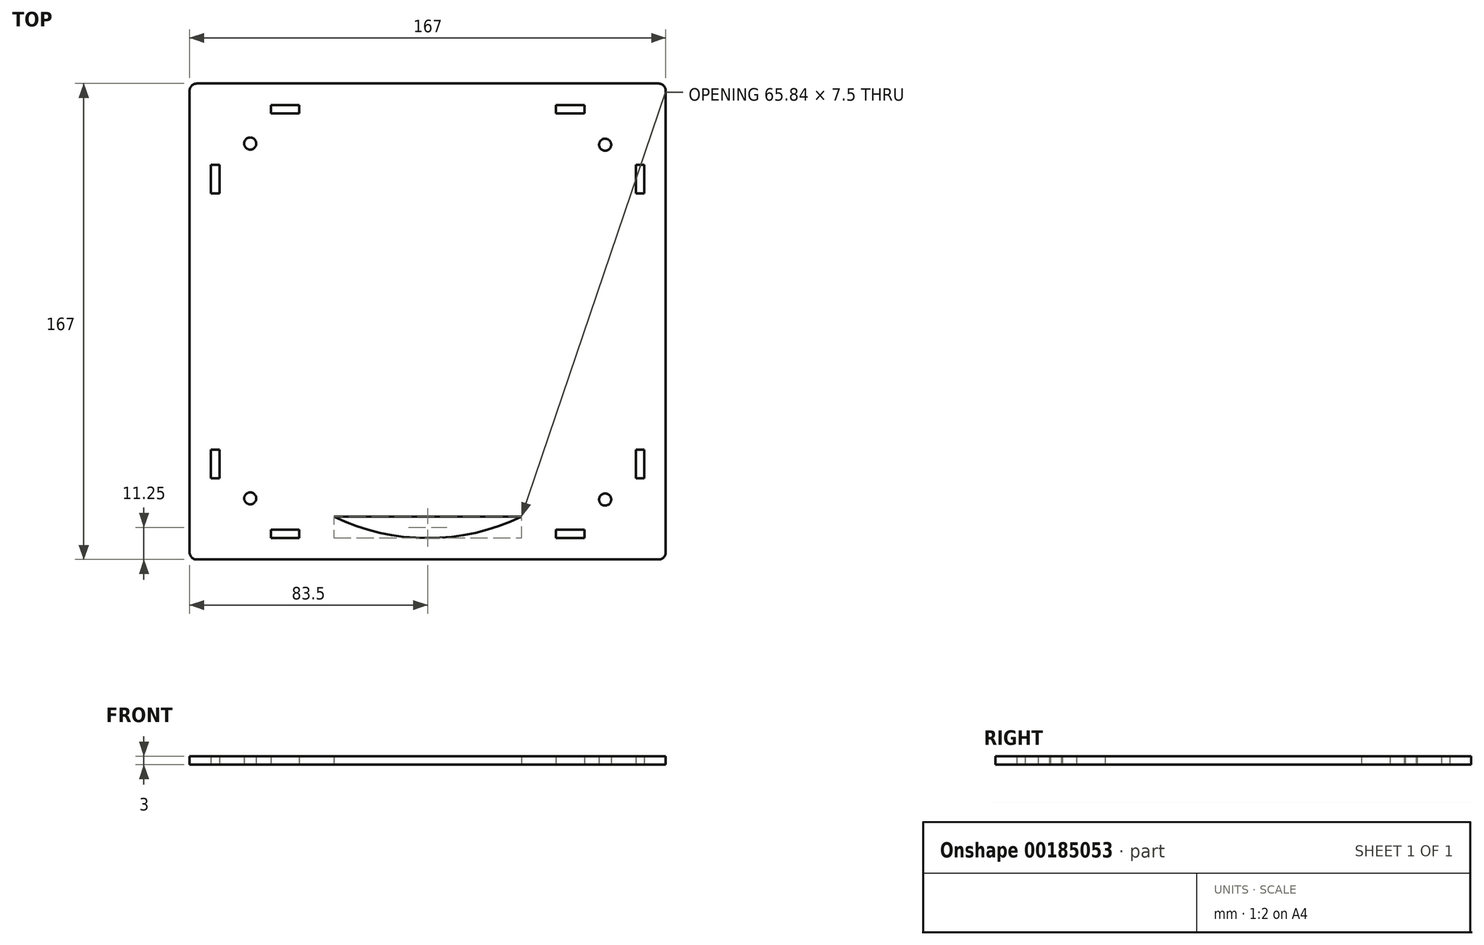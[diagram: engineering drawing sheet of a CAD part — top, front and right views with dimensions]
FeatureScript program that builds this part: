
annotation { "Feature Type Name" : "Feature", "Feature Type Description" : "" }
export const myFeature = defineFeature(function(context is Context, id is Id, definition is map)
    precondition{}
    {
        {
            var Q0;
            Q0=qCreatedBy(makeId("Top.planeOp"),FACE);
            var sketch = newSketch(context, id + "F0", { "sketchPlane" : qUnion([Q0])});
            skLineSegment(sketch, "E0.bottom", {"start": v(-81, 83.5) * mm, "end": v(81, 83.5) * mm});
            skLineSegment(sketch, "E0.top", {"start": v(-81, -83.5) * mm, "end": v(81, -83.5) * mm});
            skLineSegment(sketch, "E0.left", {"start": v(-83.5, 81) * mm, "end": v(-83.5, -81) * mm});
            skLineSegment(sketch, "E0.right", {"start": v(83.5, 81) * mm, "end": v(83.5, -81) * mm});
            skPoint(sketch, "E0.middle", {"position": v(0, 0) * mm});
            skCircle(sketch, "E1", {"center": v(0, 0) * mm, "radius": 76 * mm});
            skPoint(sketch, "E2.visualSharp", {"position": v(-83.5, 83.5) * mm});
            skArc(sketch, "E2.filletArc", {"start": v(-81, 83.5) * mm, "mid": v(-82.77, 82.77) * mm, "end": v(-83.5, 81) * mm});
            skPoint(sketch, "E3.visualSharp", {"position": v(83.5, 83.5) * mm});
            skArc(sketch, "E3.filletArc", {"start": v(83.5, 81) * mm, "mid": v(82.77, 82.77) * mm, "end": v(81, 83.5) * mm});
            skPoint(sketch, "E4.visualSharp", {"position": v(83.5, -83.5) * mm});
            skArc(sketch, "E4.filletArc", {"start": v(81, -83.5) * mm, "mid": v(82.77, -82.77) * mm, "end": v(83.5, -81) * mm});
            skPoint(sketch, "E5.visualSharp", {"position": v(-83.5, -83.5) * mm});
            skArc(sketch, "E5.filletArc", {"start": v(-83.5, -81) * mm, "mid": v(-82.77, -82.77) * mm, "end": v(-81, -83.5) * mm});
            skCircle(sketch, "E6", {"center": v(-62.25, 62.45) * mm, "radius": 2.12 * mm});
            skCircle(sketch, "E7.0.1.0", {"center": v(-62.25, -62.05) * mm, "radius": 2.12 * mm});
            skCircle(sketch, "E7.1.0.0", {"center": v(62.25, 62.05) * mm, "radius": 2.12 * mm});
            skCircle(sketch, "E7.1.1.0", {"center": v(62.25, -62.45) * mm, "radius": 2.12 * mm});
            skLineSegment(sketch, "E7.direction1", {"start": v(-62.25, 62.45) * mm, "end": v(62.25, 62.05) * mm, "construction": true});
            skLineSegment(sketch, "E7.direction2", {"start": v(-62.25, 62.45) * mm, "end": v(-62.25, -62.05) * mm, "construction": true});
            skLineSegment(sketch, "E8.bottom", {"start": v(-76, 45) * mm, "end": v(-73, 45) * mm});
            skLineSegment(sketch, "E8.top", {"start": v(-76, 55) * mm, "end": v(-73, 55) * mm});
            skLineSegment(sketch, "E8.left", {"start": v(-76, 45) * mm, "end": v(-76, 55) * mm});
            skLineSegment(sketch, "E8.right", {"start": v(-73, 45) * mm, "end": v(-73, 55) * mm});
            skLineSegment(sketch, "E9.0.1.0", {"start": v(-76, -55) * mm, "end": v(-76, -45) * mm});
            skLineSegment(sketch, "E9.0.1.1", {"start": v(-76, -45) * mm, "end": v(-73, -45) * mm});
            skLineSegment(sketch, "E9.0.1.2", {"start": v(-73, -55) * mm, "end": v(-73, -45) * mm});
            skLineSegment(sketch, "E9.0.1.3", {"start": v(-76, -55) * mm, "end": v(-73, -55) * mm});
            skLineSegment(sketch, "E9.1.0.0", {"start": v(73, 45) * mm, "end": v(73, 55) * mm});
            skLineSegment(sketch, "E9.1.0.1", {"start": v(73, 55) * mm, "end": v(76, 55) * mm});
            skLineSegment(sketch, "E9.1.0.2", {"start": v(76, 45) * mm, "end": v(76, 55) * mm});
            skLineSegment(sketch, "E9.1.0.3", {"start": v(73, 45) * mm, "end": v(76, 45) * mm});
            skLineSegment(sketch, "E9.1.1.0", {"start": v(73, -55) * mm, "end": v(73, -45) * mm});
            skLineSegment(sketch, "E9.1.1.1", {"start": v(73, -45) * mm, "end": v(76, -45) * mm});
            skLineSegment(sketch, "E9.1.1.2", {"start": v(76, -55) * mm, "end": v(76, -45) * mm});
            skLineSegment(sketch, "E9.1.1.3", {"start": v(73, -55) * mm, "end": v(76, -55) * mm});
            skLineSegment(sketch, "E9.direction1", {"start": v(-76, 45) * mm, "end": v(73, 45) * mm, "construction": true});
            skLineSegment(sketch, "E9.direction2", {"start": v(-76, 45) * mm, "end": v(-76, -55) * mm, "construction": true});
            skLineSegment(sketch, "E10.bottom", {"start": v(68.5, 68.5) * mm, "end": v(-68.5, 68.5) * mm});
            skLineSegment(sketch, "E10.top", {"start": v(68.5, -68.5) * mm, "end": v(-68.5, -68.5) * mm});
            skLineSegment(sketch, "E10.left", {"start": v(68.5, 68.5) * mm, "end": v(68.5, -68.5) * mm});
            skLineSegment(sketch, "E10.right", {"start": v(-68.5, 68.5) * mm, "end": v(-68.5, -68.5) * mm});
            skLineSegment(sketch, "E11.bottom", {"start": v(-55, 76) * mm, "end": v(-45, 76) * mm});
            skLineSegment(sketch, "E11.top", {"start": v(-55, 73) * mm, "end": v(-45, 73) * mm});
            skLineSegment(sketch, "E11.left", {"start": v(-55, 76) * mm, "end": v(-55, 73) * mm});
            skLineSegment(sketch, "E11.right", {"start": v(-45, 76) * mm, "end": v(-45, 73) * mm});
            skLineSegment(sketch, "E12.0.1.0", {"start": v(-55, -76) * mm, "end": v(-45, -76) * mm});
            skLineSegment(sketch, "E12.0.1.1", {"start": v(-55, -73) * mm, "end": v(-45, -73) * mm});
            skLineSegment(sketch, "E12.0.1.2", {"start": v(-45, -73) * mm, "end": v(-45, -76) * mm});
            skLineSegment(sketch, "E12.0.1.3", {"start": v(-55, -73) * mm, "end": v(-55, -76) * mm});
            skLineSegment(sketch, "E12.1.0.0", {"start": v(45, 73) * mm, "end": v(55, 73) * mm});
            skLineSegment(sketch, "E12.1.0.1", {"start": v(45, 76) * mm, "end": v(55, 76) * mm});
            skLineSegment(sketch, "E12.1.0.2", {"start": v(55, 76) * mm, "end": v(55, 73) * mm});
            skLineSegment(sketch, "E12.1.0.3", {"start": v(45, 76) * mm, "end": v(45, 73) * mm});
            skLineSegment(sketch, "E12.1.1.0", {"start": v(45, -76) * mm, "end": v(55, -76) * mm});
            skLineSegment(sketch, "E12.1.1.1", {"start": v(45, -73) * mm, "end": v(55, -73) * mm});
            skLineSegment(sketch, "E12.1.1.2", {"start": v(55, -73) * mm, "end": v(55, -76) * mm});
            skLineSegment(sketch, "E12.1.1.3", {"start": v(45, -73) * mm, "end": v(45, -76) * mm});
            skLineSegment(sketch, "E12.direction1", {"start": v(-55, 73) * mm, "end": v(45, 73) * mm, "construction": true});
            skLineSegment(sketch, "E12.direction2", {"start": v(-55, 73) * mm, "end": v(-55, -76) * mm, "construction": true});
            skSolve(sketch);
        }
        {
            var Q0;
            Q0=makeQuery(id+"F0.imprint","IMPRINT",FACE,{"disambiguationData":[TD([[makeQuery(id+"F0.imprint","IMPRINT",EDGE,{"derivedFrom":sQuery(id+"F0.wireOp",EDGE,"E0.bottom")}),-1.0]])]});
            var Q1;
            Q1=makeQuery(id+"F0.imprint","IMPRINT",FACE,{"disambiguationData":[TD([[makeQuery(id+"F0.imprint","IMPRINT",EDGE,{"derivedFrom":sQuery(id+"F0.wireOp",EDGE,"E7.1.0.0")}),-1.0]])]});
            var Q2;
            {var subQ0=sQuery(id+"F0.wireOp",EDGE,"E10.bottom");var subQ1=sQuery(id+"F0.wireOp",EDGE,"E1");var subQ2=makeQuery(id+"F0.imprint","INTERSECT",VERTEX,{"disambiguationData":[OD(0.0)],"derivedFrom":[subQ1,subQ0]});Q2=makeQuery(id+"F0.imprint","IMPRINT",FACE,{"disambiguationData":[TD([[makeQuery(id+"F0.imprint","IMPRINT",EDGE,{"disambiguationData":[TD([[subQ2,-1.0]])],"derivedFrom":subQ1}),1.0]])]});}
            var Q3;
            Q3=makeQuery(id+"F0.imprint","IMPRINT",FACE,{"disambiguationData":[TD([[makeQuery(id+"F0.imprint","IMPRINT",EDGE,{"derivedFrom":sQuery(id+"F0.wireOp",EDGE,"E6")}),-1.0]])]});
            var Q4;
            {var subQ0=sQuery(id+"F0.wireOp",EDGE,"E10.right");var subQ1=sQuery(id+"F0.wireOp",EDGE,"E1");var subQ2=makeQuery(id+"F0.imprint","INTERSECT",VERTEX,{"disambiguationData":[OD(0.0)],"derivedFrom":[subQ1,subQ0]});Q4=makeQuery(id+"F0.imprint","IMPRINT",FACE,{"disambiguationData":[TD([[makeQuery(id+"F0.imprint","IMPRINT",EDGE,{"disambiguationData":[TD([[subQ2,-1.0]])],"derivedFrom":subQ1}),1.0]])]});}
            var Q5;
            {var subQ0=sQuery(id+"F0.wireOp",EDGE,"E10.top");var subQ1=sQuery(id+"F0.wireOp",EDGE,"E1");var subQ2=makeQuery(id+"F0.imprint","INTERSECT",VERTEX,{"disambiguationData":[OD(0.0)],"derivedFrom":[subQ1,subQ0]});Q5=makeQuery(id+"F0.imprint","IMPRINT",FACE,{"disambiguationData":[TD([[makeQuery(id+"F0.imprint","IMPRINT",EDGE,{"disambiguationData":[TD([[subQ2,-1.0]])],"derivedFrom":subQ1}),1.0]])]});}
            var Q6;
            Q6=makeQuery(id+"F0.imprint","IMPRINT",FACE,{"disambiguationData":[TD([[makeQuery(id+"F0.imprint","IMPRINT",EDGE,{"derivedFrom":sQuery(id+"F0.wireOp",EDGE,"E7.1.1.0")}),-1.0]])]});
            var Q7;
            {var subQ0=sQuery(id+"F0.wireOp",EDGE,"E10.left");var subQ1=sQuery(id+"F0.wireOp",EDGE,"E1");var subQ2=makeQuery(id+"F0.imprint","INTERSECT",VERTEX,{"disambiguationData":[OD(0.0)],"derivedFrom":[subQ1,subQ0]});Q7=makeQuery(id+"F0.imprint","IMPRINT",FACE,{"disambiguationData":[TD([[makeQuery(id+"F0.imprint","IMPRINT",EDGE,{"disambiguationData":[TD([[subQ2,1.0]])],"derivedFrom":subQ1}),1.0]])]});}
            var Q8;
            Q8=makeQuery(id+"F0.imprint","IMPRINT",FACE,{"disambiguationData":[TD([[makeQuery(id+"F0.imprint","IMPRINT",EDGE,{"derivedFrom":sQuery(id+"F0.wireOp",EDGE,"E7.0.1.0")}),-1.0]])]});
            extrude(context, id + "F1", {"entities" : qUnion([Q0, Q1, Q2, Q3, Q4, Q5, Q6, Q7, Q8]), "depth" : 3 * mm});
        }
    });
